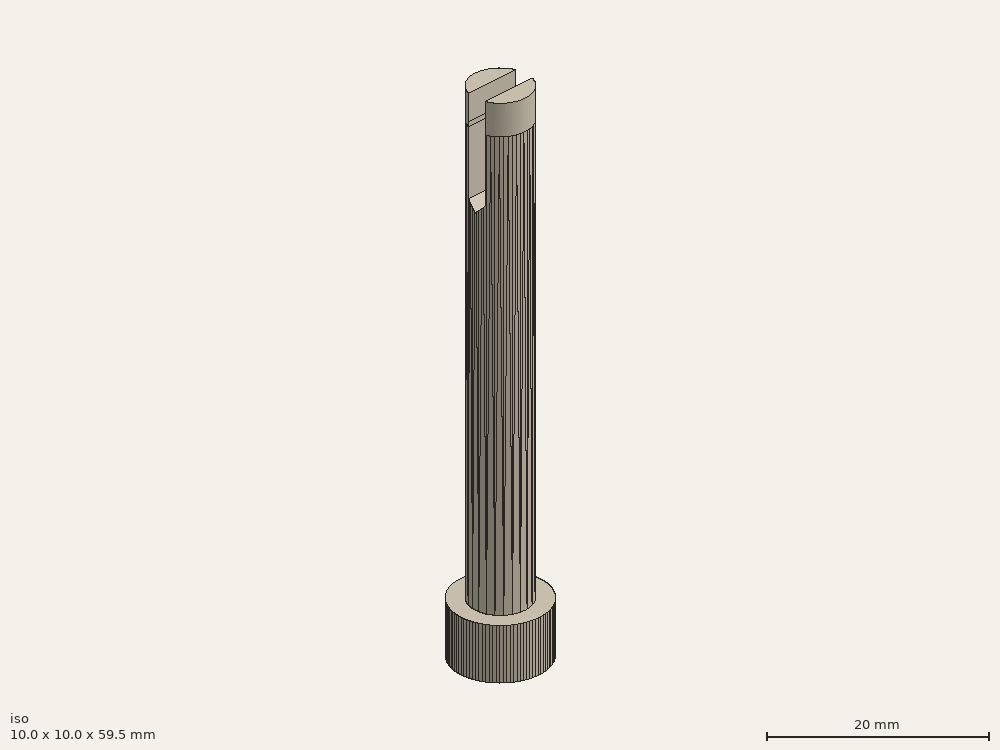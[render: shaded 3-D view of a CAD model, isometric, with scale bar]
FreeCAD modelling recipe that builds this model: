
FCSTD DOCUMENT  (FreeCAD 0.17R13522 (Git))
Label: v52_bastago_largo
License: CreativeCommons Attribution-ShareAlike
LicenseURL: http://creativecommons.org/licenses/by-sa/4.0/
objects: Part::Cut×3, Part::Box×2, Part::Chamfer×2, Part::Feature×1, Part::Cylinder×1, Part::Fuse×1
note: 10 computed .brp shape members not serialized (recipe doc carries the construction recipe); baked Part::Feature solids carry a one-line shape summary decoded from their .brp

FEATURE [Part::Feature] bastago_largo001_solid001  label="bastago_largo001 (Solid)001"
  shape: bbox 10 x 9.995 x 58.5 mm, 275 faces (baked)
FEATURE [Part::Box] Box  label="Cube"
  AttacherType = Attacher::AttachEngine3D
  Height = 10
  Length = 15
  Placement = pos=(-7,-8,-8) rot=(0,0,1;0rad)
  Width = 15
FEATURE [Part::Cut] Cut
  Base = -> bastago_largo001_solid001
  Refine = true
  Tool = -> Box
FEATURE [Part::Box] Box001  label="Cube001"
  AttacherType = Attacher::AttachEngine3D
  Height = 12
  Length = 10
  Placement = pos=(-5,-1.05,49.5) rot=(0,0,1;0rad)
  Width = 2.1
FEATURE [Part::Cut] Cut001  label="bastago con encastres"
  Base = -> Cut
  Refine = true
  Tool = -> Box001
FEATURE [Part::Cylinder] Cylinder
  Angle = 360
  AttacherType = Attacher::AttachEngine3D
  Height = 3.5
  Placement = pos=(0,0,58) rot=(0,0,1;0rad)
  Radius = 3.2
FEATURE [Part::Cut] Cut002
  Base = -> Cylinder
  Refine = true
  Tool = -> Box001
FEATURE [Part::Fuse] Fusion
  Base = -> Cut001
  Refine = true
  Tool = -> Cut002
FEATURE [Part::Chamfer] Chamfer
  Base = -> Fusion
  Edges = 1 edges r=1: [Edge532]
FEATURE [Part::Chamfer] Chamfer001
  Base = -> Chamfer
  Edges = 1 edges r=1: [Edge153]
